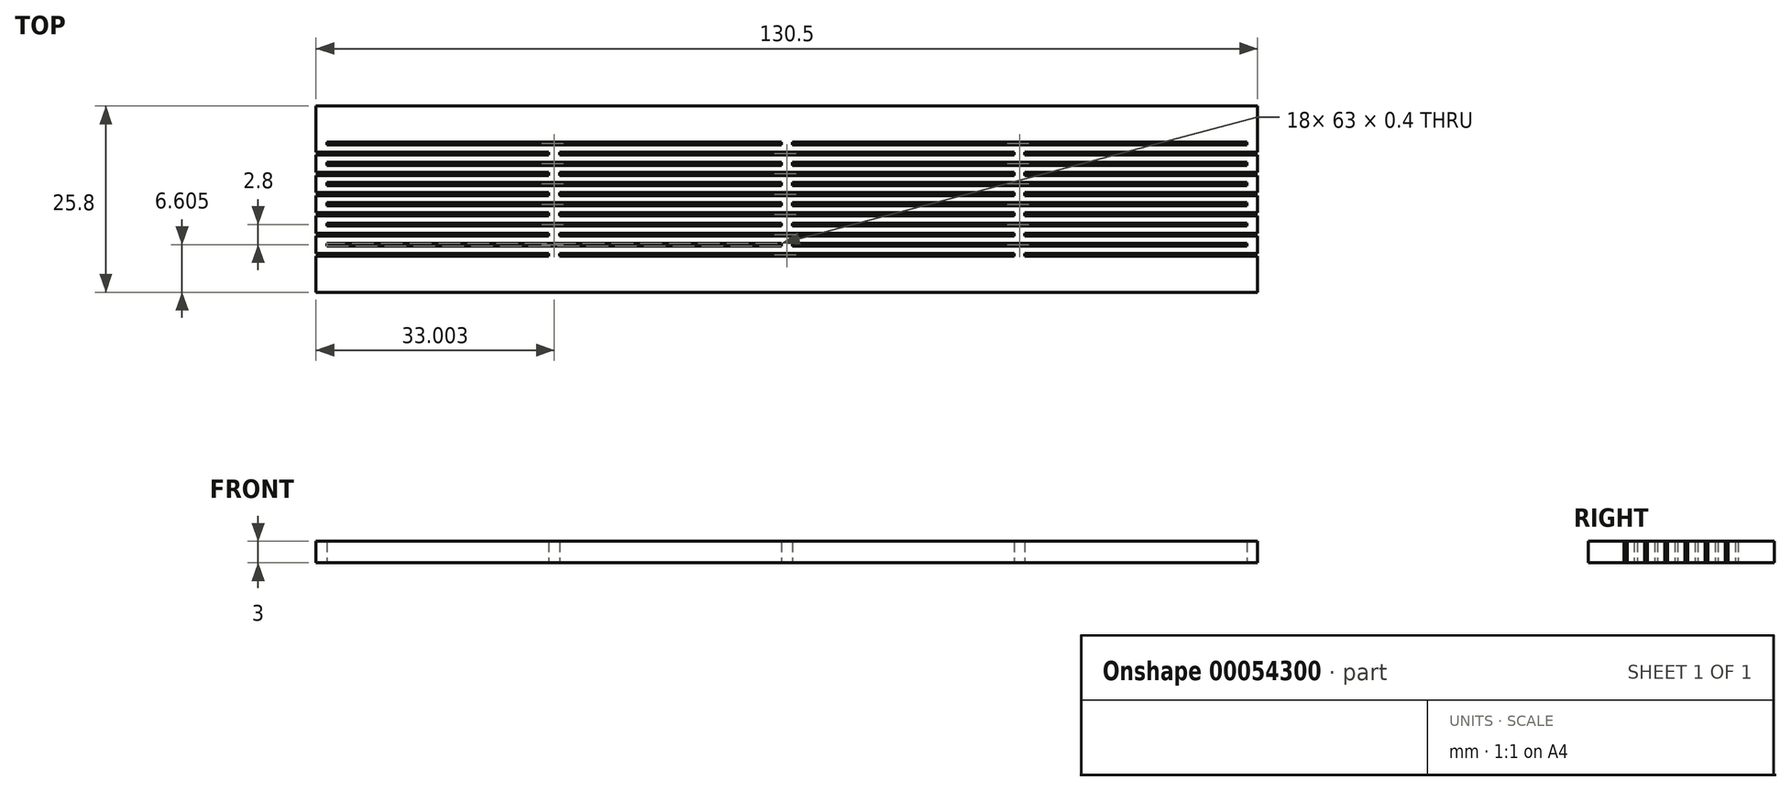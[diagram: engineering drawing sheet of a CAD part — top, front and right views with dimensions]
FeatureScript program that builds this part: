
annotation { "Feature Type Name" : "Feature", "Feature Type Description" : "" }
export const myFeature = defineFeature(function(context is Context, id is Id, definition is map)
    precondition{}
    {
        {
            var Q0;
            Q0=qCreatedBy(makeId("Top.planeOp"),FACE);
            var sketch = newSketch(context, id + "F0", { "sketchPlane" : qUnion([Q0])});
            skLineSegment(sketch, "E0.rect.bottom", {"start": v(42.26, 14.08) * mm, "end": v(-88.24, 14.08) * mm});
            skLineSegment(sketch, "E0.rect.top", {"start": v(42.26, -11.72) * mm, "end": v(-88.24, -11.72) * mm});
            skLineSegment(sketch, "E0.rect.left", {"start": v(42.26, 14.08) * mm, "end": v(42.26, -11.72) * mm});
            skLineSegment(sketch, "E0.rect.right", {"start": v(-88.24, 14.08) * mm, "end": v(-88.24, -11.72) * mm});
            skLineSegment(sketch, "E1.bottom", {"start": v(-86.74, 9.08) * mm, "end": v(-23.74, 9.08) * mm});
            skLineSegment(sketch, "E1.top", {"start": v(-86.74, 8.68) * mm, "end": v(-23.74, 8.68) * mm});
            skLineSegment(sketch, "E1.left", {"start": v(-86.74, 9.08) * mm, "end": v(-86.74, 8.68) * mm});
            skLineSegment(sketch, "E1.right", {"start": v(-23.74, 9.08) * mm, "end": v(-23.74, 8.68) * mm});
            skLineSegment(sketch, "E2.bottom", {"start": v(-22.24, 9.08) * mm, "end": v(40.76, 9.08) * mm});
            skLineSegment(sketch, "E2.top", {"start": v(-22.24, 8.68) * mm, "end": v(40.76, 8.68) * mm});
            skLineSegment(sketch, "E2.left", {"start": v(-22.24, 9.08) * mm, "end": v(-22.24, 8.68) * mm});
            skLineSegment(sketch, "E2.right", {"start": v(40.76, 9.08) * mm, "end": v(40.76, 8.68) * mm});
            skLineSegment(sketch, "E3.bottom", {"start": v(-54.49, 7.68) * mm, "end": v(8.51, 7.68) * mm});
            skLineSegment(sketch, "E3.top", {"start": v(-54.49, 7.28) * mm, "end": v(8.51, 7.28) * mm});
            skLineSegment(sketch, "E3.left", {"start": v(-54.49, 7.68) * mm, "end": v(-54.49, 7.28) * mm});
            skLineSegment(sketch, "E3.right", {"start": v(8.51, 7.68) * mm, "end": v(8.51, 7.28) * mm});
            skLineSegment(sketch, "E4.bottom", {"start": v(10.01, 7.68) * mm, "end": v(42.26, 7.68) * mm});
            skLineSegment(sketch, "E4.top", {"start": v(10.01, 7.28) * mm, "end": v(42.26, 7.28) * mm});
            skLineSegment(sketch, "E4.left", {"start": v(10.01, 7.68) * mm, "end": v(10.01, 7.28) * mm});
            skLineSegment(sketch, "E4.right", {"start": v(42.26, 7.68) * mm, "end": v(42.26, 7.28) * mm});
            skLineSegment(sketch, "E5.bottom", {"start": v(-55.99, 7.28) * mm, "end": v(-88.24, 7.28) * mm});
            skLineSegment(sketch, "E5.top", {"start": v(-55.99, 7.68) * mm, "end": v(-88.24, 7.68) * mm});
            skLineSegment(sketch, "E5.left", {"start": v(-55.99, 7.28) * mm, "end": v(-55.99, 7.68) * mm});
            skLineSegment(sketch, "E5.right", {"start": v(-88.24, 7.28) * mm, "end": v(-88.24, 7.68) * mm});
            skLineSegment(sketch, "E6.0.1.0", {"start": v(-55.99, 4.48) * mm, "end": v(-88.24, 4.48) * mm});
            skLineSegment(sketch, "E6.0.1.1", {"start": v(-54.49, 4.88) * mm, "end": v(8.51, 4.88) * mm});
            skLineSegment(sketch, "E6.0.1.2", {"start": v(10.01, 4.48) * mm, "end": v(42.26, 4.48) * mm});
            skLineSegment(sketch, "E6.0.1.3", {"start": v(-54.49, 4.48) * mm, "end": v(8.51, 4.48) * mm});
            skLineSegment(sketch, "E6.0.1.4", {"start": v(-86.74, 6.28) * mm, "end": v(-23.74, 6.28) * mm});
            skLineSegment(sketch, "E6.0.1.5", {"start": v(-86.74, 5.88) * mm, "end": v(-23.74, 5.88) * mm});
            skLineSegment(sketch, "E6.0.1.6", {"start": v(-22.24, 5.88) * mm, "end": v(40.76, 5.88) * mm});
            skLineSegment(sketch, "E6.0.1.7", {"start": v(-22.24, 6.28) * mm, "end": v(40.76, 6.28) * mm});
            skLineSegment(sketch, "E6.0.1.8", {"start": v(10.01, 4.88) * mm, "end": v(42.26, 4.88) * mm});
            skLineSegment(sketch, "E6.0.1.9", {"start": v(-55.99, 4.88) * mm, "end": v(-88.24, 4.88) * mm});
            skLineSegment(sketch, "E6.0.1.10", {"start": v(10.01, 4.88) * mm, "end": v(10.01, 4.48) * mm});
            skLineSegment(sketch, "E6.0.1.11", {"start": v(-88.24, 4.48) * mm, "end": v(-88.24, 4.88) * mm});
            skLineSegment(sketch, "E6.0.1.12", {"start": v(-55.99, 4.48) * mm, "end": v(-55.99, 4.88) * mm});
            skLineSegment(sketch, "E6.0.1.13", {"start": v(42.26, 4.88) * mm, "end": v(42.26, 4.48) * mm});
            skLineSegment(sketch, "E6.0.1.14", {"start": v(-54.49, 4.88) * mm, "end": v(-54.49, 4.48) * mm});
            skLineSegment(sketch, "E6.0.1.15", {"start": v(8.51, 4.88) * mm, "end": v(8.51, 4.48) * mm});
            skLineSegment(sketch, "E6.0.1.16", {"start": v(40.76, 6.28) * mm, "end": v(40.76, 5.88) * mm});
            skLineSegment(sketch, "E6.0.1.17", {"start": v(-22.24, 6.28) * mm, "end": v(-22.24, 5.88) * mm});
            skLineSegment(sketch, "E6.0.1.18", {"start": v(-86.74, 6.28) * mm, "end": v(-86.74, 5.88) * mm});
            skLineSegment(sketch, "E6.0.1.19", {"start": v(-23.74, 6.28) * mm, "end": v(-23.74, 5.88) * mm});
            skLineSegment(sketch, "E6.0.2.0", {"start": v(-55.99, 1.68) * mm, "end": v(-88.24, 1.68) * mm});
            skLineSegment(sketch, "E6.0.2.1", {"start": v(-54.49, 2.08) * mm, "end": v(8.51, 2.08) * mm});
            skLineSegment(sketch, "E6.0.2.2", {"start": v(10.01, 1.68) * mm, "end": v(42.26, 1.68) * mm});
            skLineSegment(sketch, "E6.0.2.3", {"start": v(-54.49, 1.68) * mm, "end": v(8.51, 1.68) * mm});
            skLineSegment(sketch, "E6.0.2.4", {"start": v(-86.74, 3.48) * mm, "end": v(-23.74, 3.48) * mm});
            skLineSegment(sketch, "E6.0.2.5", {"start": v(-86.74, 3.08) * mm, "end": v(-23.74, 3.08) * mm});
            skLineSegment(sketch, "E6.0.2.6", {"start": v(-22.24, 3.08) * mm, "end": v(40.76, 3.08) * mm});
            skLineSegment(sketch, "E6.0.2.7", {"start": v(-22.24, 3.48) * mm, "end": v(40.76, 3.48) * mm});
            skLineSegment(sketch, "E6.0.2.8", {"start": v(10.01, 2.08) * mm, "end": v(42.26, 2.08) * mm});
            skLineSegment(sketch, "E6.0.2.9", {"start": v(-55.99, 2.08) * mm, "end": v(-88.24, 2.08) * mm});
            skLineSegment(sketch, "E6.0.2.10", {"start": v(10.01, 2.08) * mm, "end": v(10.01, 1.68) * mm});
            skLineSegment(sketch, "E6.0.2.11", {"start": v(-88.24, 1.68) * mm, "end": v(-88.24, 2.08) * mm});
            skLineSegment(sketch, "E6.0.2.12", {"start": v(-55.99, 1.68) * mm, "end": v(-55.99, 2.08) * mm});
            skLineSegment(sketch, "E6.0.2.13", {"start": v(42.26, 2.08) * mm, "end": v(42.26, 1.68) * mm});
            skLineSegment(sketch, "E6.0.2.14", {"start": v(-54.49, 2.08) * mm, "end": v(-54.49, 1.68) * mm});
            skLineSegment(sketch, "E6.0.2.15", {"start": v(8.51, 2.08) * mm, "end": v(8.51, 1.68) * mm});
            skLineSegment(sketch, "E6.0.2.16", {"start": v(40.76, 3.48) * mm, "end": v(40.76, 3.08) * mm});
            skLineSegment(sketch, "E6.0.2.17", {"start": v(-22.24, 3.48) * mm, "end": v(-22.24, 3.08) * mm});
            skLineSegment(sketch, "E6.0.2.18", {"start": v(-86.74, 3.48) * mm, "end": v(-86.74, 3.08) * mm});
            skLineSegment(sketch, "E6.0.2.19", {"start": v(-23.74, 3.48) * mm, "end": v(-23.74, 3.08) * mm});
            skLineSegment(sketch, "E6.0.3.0", {"start": v(-55.99, -1.12) * mm, "end": v(-88.24, -1.12) * mm});
            skLineSegment(sketch, "E6.0.3.1", {"start": v(-54.49, -0.72) * mm, "end": v(8.51, -0.72) * mm});
            skLineSegment(sketch, "E6.0.3.2", {"start": v(10.01, -1.12) * mm, "end": v(42.26, -1.12) * mm});
            skLineSegment(sketch, "E6.0.3.3", {"start": v(-54.49, -1.12) * mm, "end": v(8.51, -1.12) * mm});
            skLineSegment(sketch, "E6.0.3.4", {"start": v(-86.74, 0.68) * mm, "end": v(-23.74, 0.68) * mm});
            skLineSegment(sketch, "E6.0.3.5", {"start": v(-86.74, 0.28) * mm, "end": v(-23.74, 0.28) * mm});
            skLineSegment(sketch, "E6.0.3.6", {"start": v(-22.24, 0.28) * mm, "end": v(40.76, 0.28) * mm});
            skLineSegment(sketch, "E6.0.3.7", {"start": v(-22.24, 0.68) * mm, "end": v(40.76, 0.68) * mm});
            skLineSegment(sketch, "E6.0.3.8", {"start": v(10.01, -0.72) * mm, "end": v(42.26, -0.72) * mm});
            skLineSegment(sketch, "E6.0.3.9", {"start": v(-55.99, -0.72) * mm, "end": v(-88.24, -0.72) * mm});
            skLineSegment(sketch, "E6.0.3.10", {"start": v(10.01, -0.72) * mm, "end": v(10.01, -1.12) * mm});
            skLineSegment(sketch, "E6.0.3.11", {"start": v(-88.24, -1.12) * mm, "end": v(-88.24, -0.72) * mm});
            skLineSegment(sketch, "E6.0.3.12", {"start": v(-55.99, -1.12) * mm, "end": v(-55.99, -0.72) * mm});
            skLineSegment(sketch, "E6.0.3.13", {"start": v(42.26, -0.72) * mm, "end": v(42.26, -1.12) * mm});
            skLineSegment(sketch, "E6.0.3.14", {"start": v(-54.49, -0.72) * mm, "end": v(-54.49, -1.12) * mm});
            skLineSegment(sketch, "E6.0.3.15", {"start": v(8.51, -0.72) * mm, "end": v(8.51, -1.12) * mm});
            skLineSegment(sketch, "E6.0.3.16", {"start": v(40.76, 0.68) * mm, "end": v(40.76, 0.28) * mm});
            skLineSegment(sketch, "E6.0.3.17", {"start": v(-22.24, 0.68) * mm, "end": v(-22.24, 0.28) * mm});
            skLineSegment(sketch, "E6.0.3.18", {"start": v(-86.74, 0.68) * mm, "end": v(-86.74, 0.28) * mm});
            skLineSegment(sketch, "E6.0.3.19", {"start": v(-23.74, 0.68) * mm, "end": v(-23.74, 0.28) * mm});
            skLineSegment(sketch, "E6.0.4.0", {"start": v(-55.99, -3.92) * mm, "end": v(-88.24, -3.92) * mm});
            skLineSegment(sketch, "E6.0.4.1", {"start": v(-54.49, -3.52) * mm, "end": v(8.51, -3.52) * mm});
            skLineSegment(sketch, "E6.0.4.2", {"start": v(10.01, -3.92) * mm, "end": v(42.26, -3.92) * mm});
            skLineSegment(sketch, "E6.0.4.3", {"start": v(-54.49, -3.92) * mm, "end": v(8.51, -3.92) * mm});
            skLineSegment(sketch, "E6.0.4.4", {"start": v(-86.74, -2.12) * mm, "end": v(-23.74, -2.12) * mm});
            skLineSegment(sketch, "E6.0.4.5", {"start": v(-86.74, -2.52) * mm, "end": v(-23.74, -2.52) * mm});
            skLineSegment(sketch, "E6.0.4.6", {"start": v(-22.24, -2.52) * mm, "end": v(40.76, -2.52) * mm});
            skLineSegment(sketch, "E6.0.4.7", {"start": v(-22.24, -2.12) * mm, "end": v(40.76, -2.12) * mm});
            skLineSegment(sketch, "E6.0.4.8", {"start": v(10.01, -3.52) * mm, "end": v(42.26, -3.52) * mm});
            skLineSegment(sketch, "E6.0.4.9", {"start": v(-55.99, -3.52) * mm, "end": v(-88.24, -3.52) * mm});
            skLineSegment(sketch, "E6.0.4.10", {"start": v(10.01, -3.52) * mm, "end": v(10.01, -3.92) * mm});
            skLineSegment(sketch, "E6.0.4.11", {"start": v(-88.24, -3.92) * mm, "end": v(-88.24, -3.52) * mm});
            skLineSegment(sketch, "E6.0.4.12", {"start": v(-55.99, -3.92) * mm, "end": v(-55.99, -3.52) * mm});
            skLineSegment(sketch, "E6.0.4.13", {"start": v(42.26, -3.52) * mm, "end": v(42.26, -3.92) * mm});
            skLineSegment(sketch, "E6.0.4.14", {"start": v(-54.49, -3.52) * mm, "end": v(-54.49, -3.92) * mm});
            skLineSegment(sketch, "E6.0.4.15", {"start": v(8.51, -3.52) * mm, "end": v(8.51, -3.92) * mm});
            skLineSegment(sketch, "E6.0.4.16", {"start": v(40.76, -2.12) * mm, "end": v(40.76, -2.52) * mm});
            skLineSegment(sketch, "E6.0.4.17", {"start": v(-22.24, -2.12) * mm, "end": v(-22.24, -2.52) * mm});
            skLineSegment(sketch, "E6.0.4.18", {"start": v(-86.74, -2.12) * mm, "end": v(-86.74, -2.52) * mm});
            skLineSegment(sketch, "E6.0.4.19", {"start": v(-23.74, -2.12) * mm, "end": v(-23.74, -2.52) * mm});
            skLineSegment(sketch, "E6.0.5.0", {"start": v(-55.99, -6.72) * mm, "end": v(-88.24, -6.72) * mm});
            skLineSegment(sketch, "E6.0.5.1", {"start": v(-54.49, -6.32) * mm, "end": v(8.51, -6.32) * mm});
            skLineSegment(sketch, "E6.0.5.2", {"start": v(10.01, -6.72) * mm, "end": v(42.26, -6.72) * mm});
            skLineSegment(sketch, "E6.0.5.3", {"start": v(-54.49, -6.72) * mm, "end": v(8.51, -6.72) * mm});
            skLineSegment(sketch, "E6.0.5.4", {"start": v(-86.74, -4.92) * mm, "end": v(-23.74, -4.92) * mm});
            skLineSegment(sketch, "E6.0.5.5", {"start": v(-86.74, -5.32) * mm, "end": v(-23.74, -5.32) * mm});
            skLineSegment(sketch, "E6.0.5.6", {"start": v(-22.24, -5.32) * mm, "end": v(40.76, -5.32) * mm});
            skLineSegment(sketch, "E6.0.5.7", {"start": v(-22.24, -4.92) * mm, "end": v(40.76, -4.92) * mm});
            skLineSegment(sketch, "E6.0.5.8", {"start": v(10.01, -6.32) * mm, "end": v(42.26, -6.32) * mm});
            skLineSegment(sketch, "E6.0.5.9", {"start": v(-55.99, -6.32) * mm, "end": v(-88.24, -6.32) * mm});
            skLineSegment(sketch, "E6.0.5.10", {"start": v(10.01, -6.32) * mm, "end": v(10.01, -6.72) * mm});
            skLineSegment(sketch, "E6.0.5.11", {"start": v(-88.24, -6.72) * mm, "end": v(-88.24, -6.32) * mm});
            skLineSegment(sketch, "E6.0.5.12", {"start": v(-55.99, -6.72) * mm, "end": v(-55.99, -6.32) * mm});
            skLineSegment(sketch, "E6.0.5.13", {"start": v(42.26, -6.32) * mm, "end": v(42.26, -6.72) * mm});
            skLineSegment(sketch, "E6.0.5.14", {"start": v(-54.49, -6.32) * mm, "end": v(-54.49, -6.72) * mm});
            skLineSegment(sketch, "E6.0.5.15", {"start": v(8.51, -6.32) * mm, "end": v(8.51, -6.72) * mm});
            skLineSegment(sketch, "E6.0.5.16", {"start": v(40.76, -4.92) * mm, "end": v(40.76, -5.32) * mm});
            skLineSegment(sketch, "E6.0.5.17", {"start": v(-22.24, -4.92) * mm, "end": v(-22.24, -5.32) * mm});
            skLineSegment(sketch, "E6.0.5.18", {"start": v(-86.74, -4.92) * mm, "end": v(-86.74, -5.32) * mm});
            skLineSegment(sketch, "E6.0.5.19", {"start": v(-23.74, -4.92) * mm, "end": v(-23.74, -5.32) * mm});
            skLineSegment(sketch, "E6.direction1", {"start": v(-88.24, 7.28) * mm, "end": v(61.76, 7.28) * mm, "construction": true});
            skLineSegment(sketch, "E6.direction2", {"start": v(-88.24, 7.28) * mm, "end": v(-88.24, 4.48) * mm, "construction": true});
            skSolve(sketch);
        }
        {
            var Q0;
            {var subQ65=sQuery(id+"F0.wireOp",EDGE,"E0.rect.bottom");Q0=makeQuery(id+"F0.imprint","IMPRINT",FACE,{"disambiguationData":[TD([[makeQuery(id+"F0.imprint","IMPRINT",EDGE,{"derivedFrom":subQ65}),1.0]])]});}
            var Q1;
            Q1 = qConstructionFilter(qBodyType(qCreatedBy(id + "F0" ,EDGE), BodyType.WIRE), ConstructionObject.NO);
            extrude(context, id + "F1", {"entities" : qUnion([Q0]), "surfaceEntities" : qUnion([Q1]), "depth" : 3 * mm});
        }
    });
